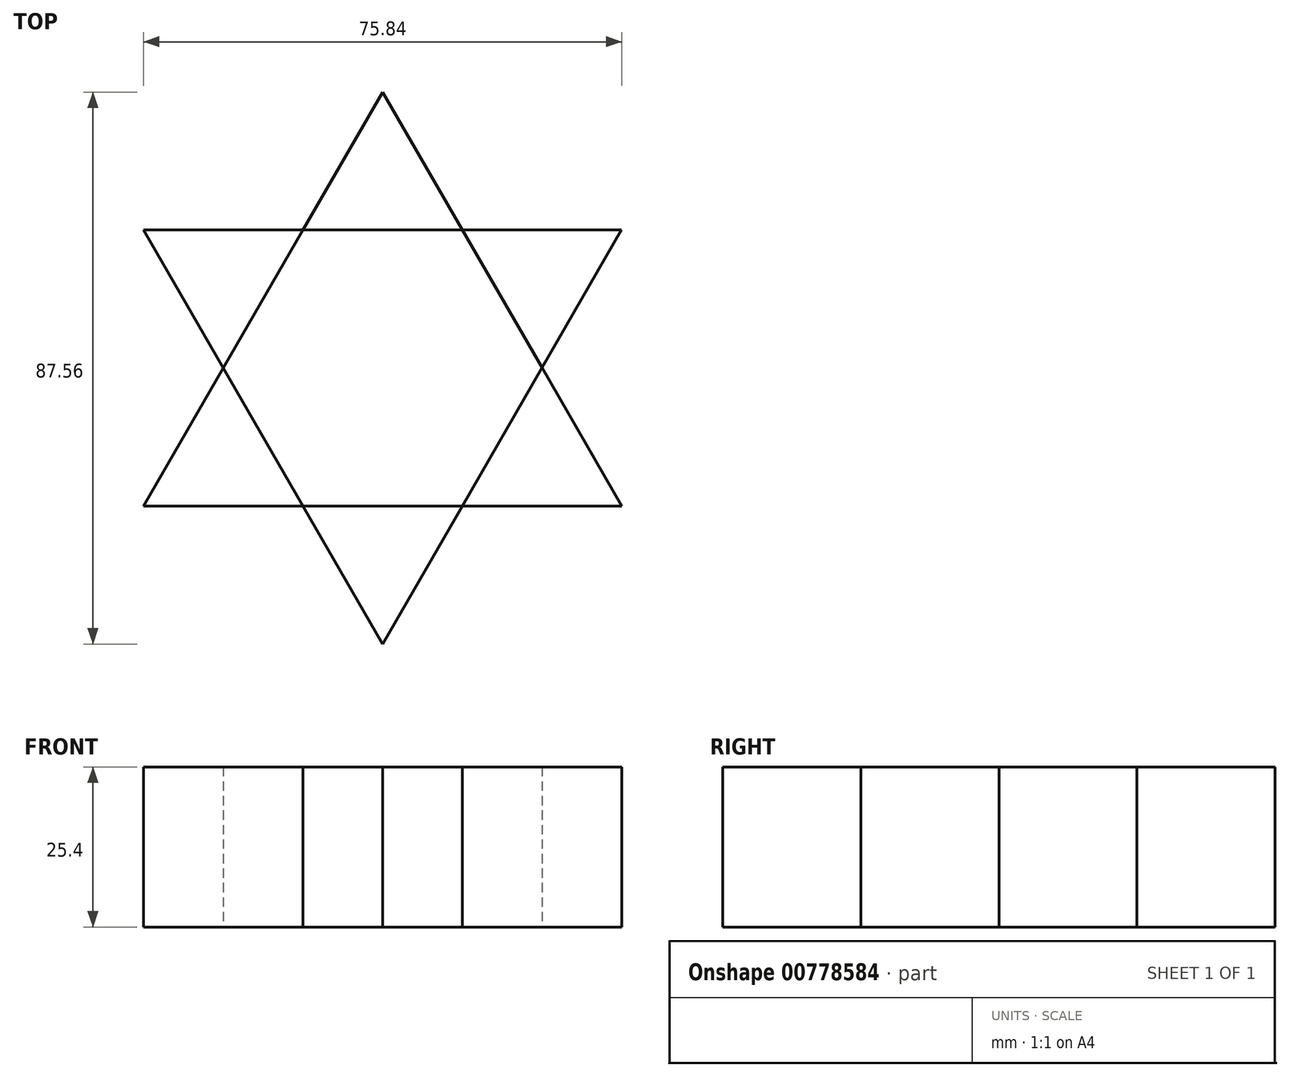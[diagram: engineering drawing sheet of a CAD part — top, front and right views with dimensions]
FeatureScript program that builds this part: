
annotation { "Feature Type Name" : "Feature", "Feature Type Description" : "" }
export const myFeature = defineFeature(function(context is Context, id is Id, definition is map)
    precondition{}
    {
        {
            var Q0;
            Q0=qCreatedBy(makeId("Top.planeOp"),FACE);
            var sketch = newSketch(context, id + "F0", { "sketchPlane" : qUnion([Q0])});
            skCircle(sketch, "E0.cCircle", {"center": v(0, 0) * mm, "radius": 37.92 * mm, "construction": true});
            skLineSegment(sketch, "E0.0", {"start": v(-37.92, -21.9) * mm, "end": v(-37.92, 21.9) * mm});
            skLineSegment(sketch, "E0.1", {"start": v(-37.92, 21.9) * mm, "end": v(0, 43.78) * mm});
            skLineSegment(sketch, "E0.2", {"start": v(0, 43.78) * mm, "end": v(37.92, 21.9) * mm});
            skLineSegment(sketch, "E0.3", {"start": v(37.92, 21.9) * mm, "end": v(37.92, -21.9) * mm});
            skLineSegment(sketch, "E0.4", {"start": v(37.92, -21.9) * mm, "end": v(0, -43.78) * mm});
            skLineSegment(sketch, "E0.5", {"start": v(0, -43.78) * mm, "end": v(-37.92, -21.9) * mm});
            skPoint(sketch, "E0.0.midPoint", {"position": v(-37.92, 0) * mm});
            skSolve(sketch);
        }
        {
            var Q0;
            Q0=qCreatedBy(makeId("Top.planeOp"),FACE);
            var sketch = newSketch(context, id + "F1", { "sketchPlane" : qUnion([Q0])});
            skLineSegment(sketch, "E1", {"start": v(-37.92, 21.9) * mm, "end": v(37.85, 21.9) * mm});
            skLineSegment(sketch, "E2", {"start": v(0, 43.78) * mm, "end": v(-37.92, -21.9) * mm});
            skLineSegment(sketch, "E3", {"start": v(-37.92, -21.9) * mm, "end": v(37.92, -21.9) * mm});
            skLineSegment(sketch, "E4", {"start": v(0, 43.78) * mm, "end": v(37.92, -21.9) * mm});
            skLineSegment(sketch, "E5", {"start": v(-37.92, 21.9) * mm, "end": v(0, -43.78) * mm});
            skLineSegment(sketch, "E6", {"start": v(0, -43.78) * mm, "end": v(37.85, 21.9) * mm});
            skSolve(sketch);
        }
        {
            var Q0;
            {var subQ0=sQuery(id+"F1.wireOp",EDGE,"E4");var subQ1=sQuery(id+"F1.wireOp",EDGE,"E3");var subQ2=makeQuery(id+"F1.imprint","INTERSECT",VERTEX,{"derivedFrom":[subQ1,subQ0]});Q0=makeQuery(id+"F1.imprint","IMPRINT",FACE,{"disambiguationData":[TD([[makeQuery(id+"F1.imprint","IMPRINT",EDGE,{"disambiguationData":[TD([[subQ2,1.0]])],"derivedFrom":subQ1}),1.0]])]});}
            var Q1;
            {var subQ0=sQuery(id+"F1.wireOp",EDGE,"E6");var subQ1=sQuery(id+"F1.wireOp",EDGE,"E1");var subQ2=makeQuery(id+"F1.imprint","INTERSECT",VERTEX,{"derivedFrom":[subQ1,subQ0]});Q1=makeQuery(id+"F1.imprint","IMPRINT",FACE,{"disambiguationData":[TD([[makeQuery(id+"F1.imprint","IMPRINT",EDGE,{"disambiguationData":[TD([[subQ2,1.0]])],"derivedFrom":subQ1}),-1.0]])]});}
            var Q2;
            {var subQ0=sQuery(id+"F1.wireOp",EDGE,"E2");var subQ1=sQuery(id+"F1.wireOp",EDGE,"E1");var subQ2=makeQuery(id+"F1.imprint","INTERSECT",VERTEX,{"derivedFrom":[subQ1,subQ0]});Q2=makeQuery(id+"F1.imprint","IMPRINT",FACE,{"disambiguationData":[TD([[makeQuery(id+"F1.imprint","IMPRINT",EDGE,{"disambiguationData":[TD([[subQ2,-1.0]])],"derivedFrom":subQ1}),1.0]])]});}
            var Q3;
            {var subQ0=sQuery(id+"F1.wireOp",EDGE,"E5");var subQ1=sQuery(id+"F1.wireOp",EDGE,"E1");var subQ2=makeQuery(id+"F1.imprint","INTERSECT",VERTEX,{"derivedFrom":[subQ1,subQ0]});Q3=makeQuery(id+"F1.imprint","IMPRINT",FACE,{"disambiguationData":[TD([[makeQuery(id+"F1.imprint","IMPRINT",EDGE,{"disambiguationData":[TD([[subQ2,-1.0]])],"derivedFrom":subQ1}),-1.0]])]});}
            var Q4;
            {var subQ0=sQuery(id+"F1.wireOp",EDGE,"E3");var subQ1=sQuery(id+"F1.wireOp",EDGE,"E2");var subQ2=makeQuery(id+"F1.imprint","INTERSECT",VERTEX,{"derivedFrom":[subQ1,subQ0]});Q4=makeQuery(id+"F1.imprint","IMPRINT",FACE,{"disambiguationData":[TD([[makeQuery(id+"F1.imprint","IMPRINT",EDGE,{"disambiguationData":[TD([[subQ2,1.0]])],"derivedFrom":subQ1}),1.0]])]});}
            var Q5;
            {var subQ0=sQuery(id+"F1.wireOp",EDGE,"E5");var subQ1=sQuery(id+"F1.wireOp",EDGE,"E3");var subQ2=makeQuery(id+"F1.imprint","INTERSECT",VERTEX,{"derivedFrom":[subQ1,subQ0]});Q5=makeQuery(id+"F1.imprint","IMPRINT",FACE,{"disambiguationData":[TD([[makeQuery(id+"F1.imprint","IMPRINT",EDGE,{"disambiguationData":[TD([[subQ2,-1.0]])],"derivedFrom":subQ1}),-1.0]])]});}
            extrude(context, id + "F2", {"entities" : qUnion([Q0, Q1, Q2, Q3, Q4, Q5]), "endBound" : BoundingType.SYMMETRIC, "depth" : 25.4 * mm, "offsetDistance" : 25.4 * mm});
        }
    });
